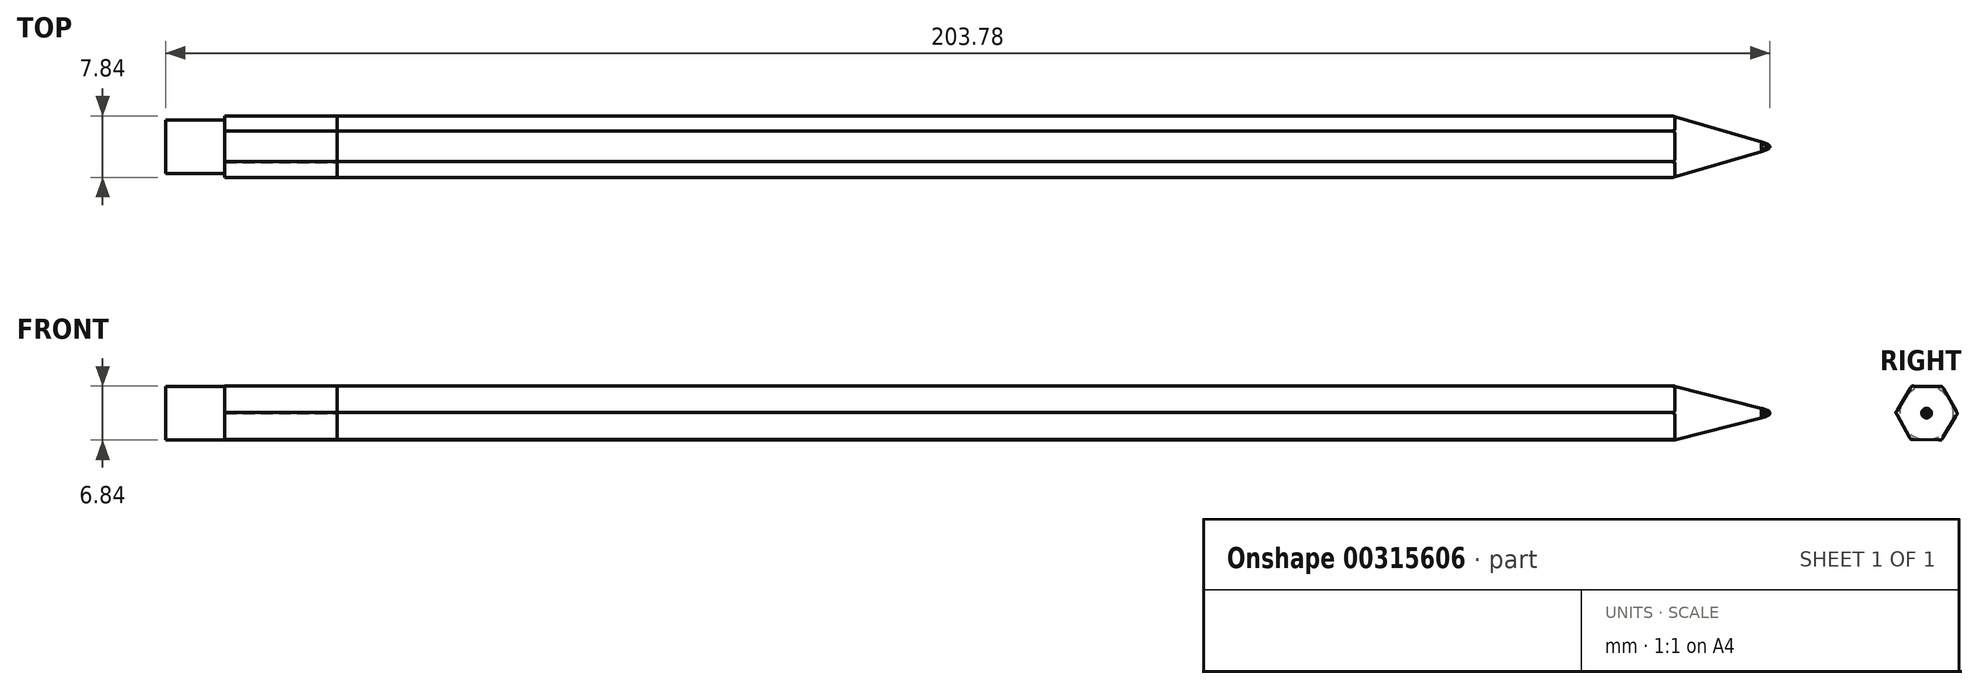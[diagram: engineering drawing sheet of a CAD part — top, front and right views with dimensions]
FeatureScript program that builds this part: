
annotation { "Feature Type Name" : "Feature", "Feature Type Description" : "" }
export const myFeature = defineFeature(function(context is Context, id is Id, definition is map)
    precondition{}
    {
        {
            var Q0;
            Q0=qCreatedBy(makeId("Right.planeOp"),FACE);
            var sketch = newSketch(context, id + "F0", { "sketchPlane" : qUnion([Q0])});
            skCircle(sketch, "E0.cCircle", {"center": v(0, 0) * mm, "radius": 3.92 * mm, "construction": true});
            skLineSegment(sketch, "E0.0", {"start": v(2, 3.36) * mm, "end": v(3.92, -0.06) * mm});
            skLineSegment(sketch, "E0.1", {"start": v(3.92, -0.06) * mm, "end": v(1.9, -3.42) * mm});
            skLineSegment(sketch, "E0.2", {"start": v(1.9, -3.42) * mm, "end": v(-2, -3.36) * mm});
            skLineSegment(sketch, "E0.3", {"start": v(-2, -3.36) * mm, "end": v(-3.92, 0.06) * mm});
            skLineSegment(sketch, "E0.4", {"start": v(-3.92, 0.06) * mm, "end": v(-1.9, 3.42) * mm});
            skLineSegment(sketch, "E0.5", {"start": v(-1.9, 3.42) * mm, "end": v(2, 3.36) * mm});
            skSolve(sketch);
        }
        {
            var Q0;
            Q0=makeQuery(id+"F0.imprint","IMPRINT",FACE,{"disambiguationData":[TD([[makeQuery(id+"F0.imprint","IMPRINT",EDGE,{"derivedFrom":sQuery(id+"F0.wireOp",EDGE,"E0.0")}),-1.0]])]});
            extrude(context, id + "F1", {"entities" : qUnion([Q0]), "depth" : 88.98 * mm});
        }
        {
            var Q0;
            Q0=qCreatedBy(makeId("Top.planeOp"),FACE);
            var sketch = newSketch(context, id + "F2", { "sketchPlane" : qUnion([Q0])});
            skLineSegment(sketch, "E1", {"start": v(0, 0) * mm, "end": v(-80.95, 0) * mm});
            skLineSegment(sketch, "E2", {"start": v(0, 0) * mm, "end": v(102.36, 0) * mm});
            skSolve(sketch);
        }
        {
            var Q0;
            Q0=makeQuery(id+"F1.opExtrude","CAP_FACE",FACE,{"disambiguationData":[OSD([sQuery(id+"F0.wireOp",EDGE,"E0.0"),sQuery(id+"F0.wireOp",EDGE,"E0.1"),sQuery(id+"F0.wireOp",EDGE,"E0.2"),sQuery(id+"F0.wireOp",EDGE,"E0.3"),sQuery(id+"F0.wireOp",EDGE,"E0.4"),sQuery(id+"F0.wireOp",EDGE,"E0.5")])],"isStart":true});
            extrude(context, id + "F3", {"entities" : qUnion([Q0]), "operationType" : NewBodyOperationType.ADD, "depth" : 80.95 * mm});
        }
        {
            var Q1;
            Q1=makeQuery(id+"F1.opExtrude","CAP_FACE",FACE,{"disambiguationData":[OSD([sQuery(id+"F0.wireOp",EDGE,"E0.0"),sQuery(id+"F0.wireOp",EDGE,"E0.1"),sQuery(id+"F0.wireOp",EDGE,"E0.2"),sQuery(id+"F0.wireOp",EDGE,"E0.3"),sQuery(id+"F0.wireOp",EDGE,"E0.4"),sQuery(id+"F0.wireOp",EDGE,"E0.5")])],"isStart":false});
            var Q2;
            Q2=sQuery(id+"F2.wireOp",VERTEX,"E2.end");
            loft(context, id + "F4", {"operationType" : NewBodyOperationType.ADD, "sheetProfilesArray" : [{ "sheetProfileEntities" : qUnion([Q1]) }, { "sheetProfileEntities" : qUnion([Q2]) }]});
        }
        {
            var Q0;
            Q0=makeQuery(id+"F3.opExtrude","CAP_FACE",FACE,{"disambiguationData":[OSD([sQuery(id+"F0.wireOp",EDGE,"E0.0"),sQuery(id+"F0.wireOp",EDGE,"E0.1"),sQuery(id+"F0.wireOp",EDGE,"E0.2"),sQuery(id+"F0.wireOp",EDGE,"E0.3"),sQuery(id+"F0.wireOp",EDGE,"E0.4"),sQuery(id+"F0.wireOp",EDGE,"E0.5")])],"isStart":false});
            extrude(context, id + "F5", {"entities" : qUnion([Q0]), "depth" : 14.3 * mm});
        }
        {
            var Q0;
            Q0=makeQuery(id+"F4.opLoft","SWEPT_EDGE",EDGE,{"disambiguationData":[OSD([sQuery(id+"F0.wireOp",EDGE,"E0.3"),sQuery(id+"F0.wireOp",EDGE,"E0.4"),sQuery(id+"F2.wireOp",VERTEX,"E2.end")])]});
            var Q1;
            Q1=makeQuery(id+"F4.opLoft","SWEPT_EDGE",EDGE,{"disambiguationData":[OSD([sQuery(id+"F0.wireOp",EDGE,"E0.1"),sQuery(id+"F0.wireOp",EDGE,"E0.2"),sQuery(id+"F2.wireOp",VERTEX,"E2.end")])]});
            var Q2;
            Q2=makeQuery(id+"F4.opLoft","SWEPT_EDGE",EDGE,{"disambiguationData":[OSD([sQuery(id+"F0.wireOp",EDGE,"E0.2"),sQuery(id+"F0.wireOp",EDGE,"E0.3"),sQuery(id+"F2.wireOp",VERTEX,"E2.end")])]});
            var Q3;
            Q3=makeQuery(id+"F4.opLoft","SWEPT_EDGE",EDGE,{"disambiguationData":[OSD([sQuery(id+"F0.wireOp",EDGE,"E0.0"),sQuery(id+"F0.wireOp",EDGE,"E0.1"),sQuery(id+"F2.wireOp",VERTEX,"E2.end")])]});
            var Q4;
            Q4=makeQuery(id+"F4.opLoft","SWEPT_EDGE",EDGE,{"disambiguationData":[OSD([sQuery(id+"F0.wireOp",EDGE,"E0.0"),sQuery(id+"F0.wireOp",EDGE,"E0.5"),sQuery(id+"F2.wireOp",VERTEX,"E2.end")])]});
            var Q5;
            Q5=makeQuery(id+"F4.opLoft","SWEPT_EDGE",EDGE,{"disambiguationData":[OSD([sQuery(id+"F0.wireOp",EDGE,"E0.4"),sQuery(id+"F0.wireOp",EDGE,"E0.5"),sQuery(id+"F2.wireOp",VERTEX,"E2.end")])]});
            fillet(context, id + "F6", {"entities" : qUnion([Q0, Q1, Q2, Q3, Q4, Q5]), "radius" : 0.64 * mm, "tangentPropagation" : true, "allowEdgeOverflow" : false});
        }
        {
            var Q0;
            Q0=makeQuery(id+"F5.opExtrude","CAP_FACE",FACE,{"disambiguationData":[OSD([sQuery(id+"F0.wireOp",EDGE,"E0.0"),sQuery(id+"F0.wireOp",EDGE,"E0.1"),sQuery(id+"F0.wireOp",EDGE,"E0.2"),sQuery(id+"F0.wireOp",EDGE,"E0.3"),sQuery(id+"F0.wireOp",EDGE,"E0.4"),sQuery(id+"F0.wireOp",EDGE,"E0.5")])],"isStart":false});
            var sketch = newSketch(context, id + "F7", { "sketchPlane" : qUnion([Q0])});
            skCircle(sketch, "E3", {"center": v(0, 0) * mm, "radius": 3.4 * mm});
            skSolve(sketch);
        }
        {
            var Q0;
            {var subQ0=sQuery(id+"F7.wireOp",EDGE,"E3");var subQ4=makeQuery(id+"F7.imprint","INTERSECT",VERTEX,{"derivedFrom":[makeQuery(id+"F5.opExtrude","CAP_EDGE",EDGE,{"disambiguationData":[OSD([sQuery(id+"F0.wireOp",EDGE,"E0.5")])],"isStart":false}),subQ0]});Q0=makeQuery(id+"F7.imprint","IMPRINT",FACE,{"disambiguationData":[TD([[makeQuery(id+"F7.imprint","IMPRINT",EDGE,{"disambiguationData":[TD([[subQ4,1.0]])],"derivedFrom":subQ0}),1.0]])]});}
            extrude(context, id + "F8", {"entities" : qUnion([Q0]), "depth" : 7.52 * mm});
        }
    });
